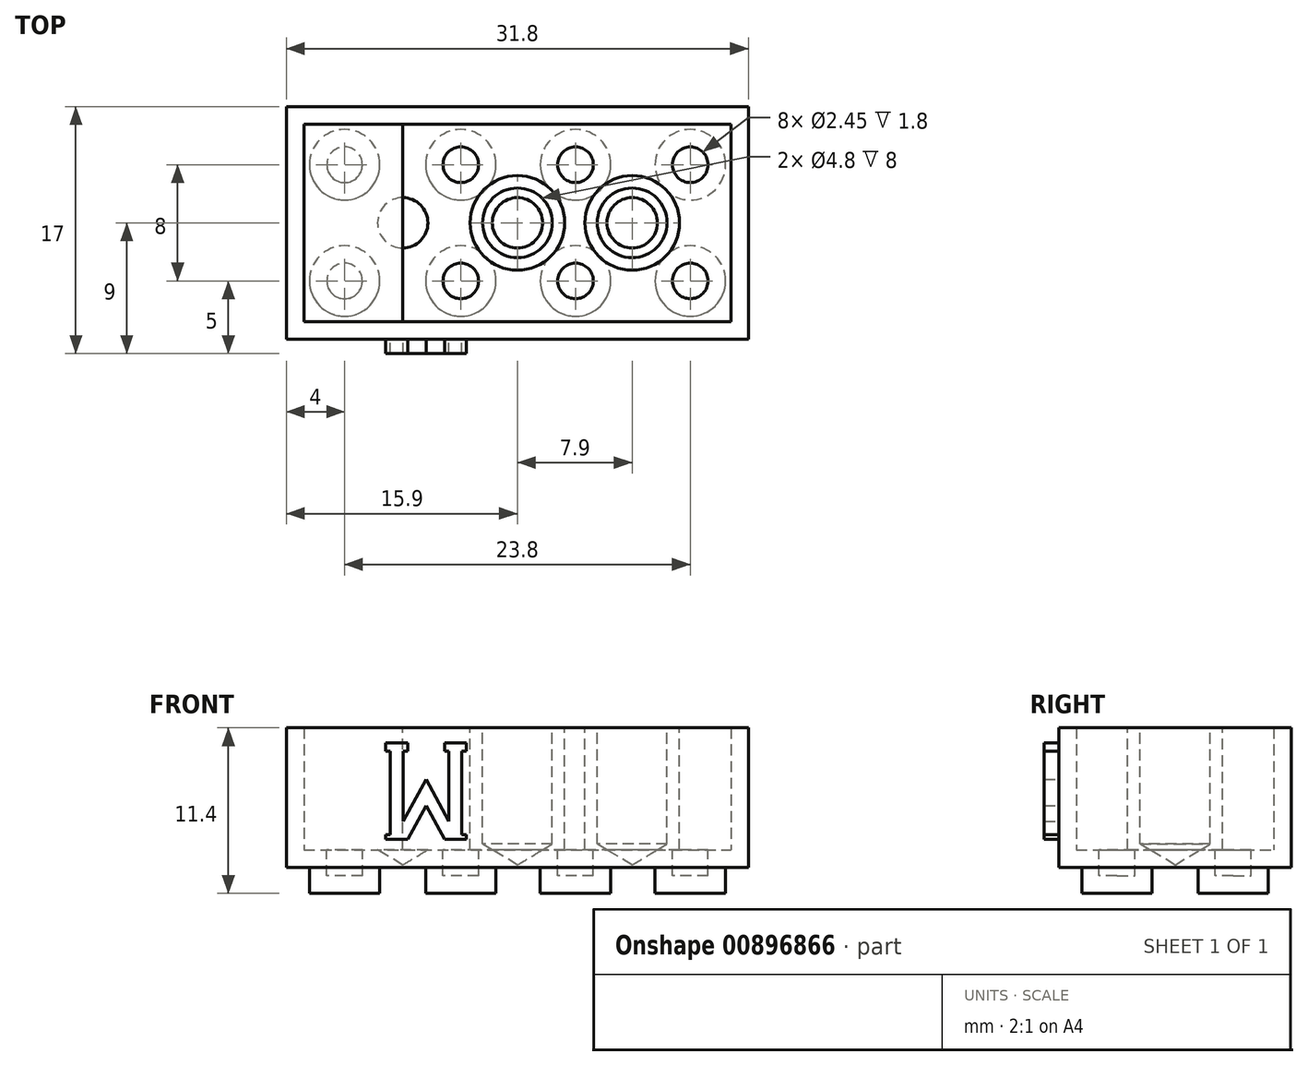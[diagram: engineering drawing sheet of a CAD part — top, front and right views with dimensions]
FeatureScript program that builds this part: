
annotation { "Feature Type Name" : "Feature", "Feature Type Description" : "" }
export const myFeature = defineFeature(function(context is Context, id is Id, definition is map)
    precondition{}
    {
        {
            var Q0;
            Q0=qCreatedBy(makeId("Front.planeOp"),FACE);
            var sketch = newSketch(context, id + "F0", { "sketchPlane" : qUnion([Q0])});
            skLineSegment(sketch, "E0.bottom", {"start": v(-9.6, 5.02) * mm, "end": v(22.2, 5.02) * mm});
            skLineSegment(sketch, "E0.top", {"start": v(-9.6, -4.58) * mm, "end": v(22.2, -4.58) * mm});
            skLineSegment(sketch, "E0.left", {"start": v(-9.6, 5.02) * mm, "end": v(-9.6, -4.58) * mm});
            skLineSegment(sketch, "E0.right", {"start": v(22.2, 5.02) * mm, "end": v(22.2, -4.58) * mm});
            skSolve(sketch);
        }
        {
            var Q0;
            Q0=makeQuery(id+"F0.imprint","IMPRINT",FACE,{"disambiguationData":[TD([[makeQuery(id+"F0.imprint","IMPRINT",EDGE,{"derivedFrom":sQuery(id+"F0.wireOp",EDGE,"E0.bottom")}),-1.0]])]});
            extrude(context, id + "F1", {"entities" : qUnion([Q0]), "depth" : 16 * mm, "offsetDistance" : 25 * mm});
        }
        {
            var Q0;
            Q0=makeQuery(id+"F1.opExtrude","SWEPT_FACE",FACE,{"disambiguationData":[OSD([sQuery(id+"F0.wireOp",EDGE,"E0.top")])]});
            var sketch = newSketch(context, id + "F2", { "sketchPlane" : qUnion([Q0])});
            skLineSegment(sketch, "E1", {"start": v(6.3, 0) * mm, "end": v(6.3, 16) * mm});
            skLineSegment(sketch, "E2", {"start": v(22.2, 8) * mm, "end": v(-9.6, 8) * mm});
            skLineSegment(sketch, "E3", {"start": v(14.2, 0) * mm, "end": v(14.2, 16) * mm});
            skLineSegment(sketch, "E4", {"start": v(-1.6, 0) * mm, "end": v(-1.6, 16) * mm});
            skLineSegment(sketch, "E5", {"start": v(22.2, 4) * mm, "end": v(20.62, 4) * mm});
            skLineSegment(sketch, "E6", {"start": v(22.22, 12) * mm, "end": v(20.62, 12) * mm});
            skCircle(sketch, "E7", {"center": v(18.2, 4) * mm, "radius": 2.43 * mm});
            skCircle(sketch, "E8", {"center": v(2.4, 4) * mm, "radius": 2.43 * mm});
            skCircle(sketch, "E9", {"center": v(18.2, 12) * mm, "radius": 2.43 * mm});
            skCircle(sketch, "E10", {"center": v(2.4, 12) * mm, "radius": 2.43 * mm});
            skCircle(sketch, "E11", {"center": v(10.3, 12) * mm, "radius": 2.43 * mm});
            skCircle(sketch, "E12", {"center": v(10.3, 4) * mm, "radius": 2.43 * mm});
            skCircle(sketch, "E13", {"center": v(-5.6, 4) * mm, "radius": 2.43 * mm});
            skCircle(sketch, "E14", {"center": v(-5.6, 12) * mm, "radius": 2.43 * mm});
            skLineSegment(sketch, "E15.trimOffspring", {"start": v(15.77, 4) * mm, "end": v(12.72, 4) * mm});
            skLineSegment(sketch, "E16.trimOffspring", {"start": v(7.87, 4) * mm, "end": v(4.82, 4) * mm});
            skLineSegment(sketch, "E17.trimOffspring", {"start": v(-0.03, 4) * mm, "end": v(-3.18, 4) * mm});
            skLineSegment(sketch, "E18.trimOffspring", {"start": v(-8.03, 4) * mm, "end": v(-9.6, 4) * mm});
            skLineSegment(sketch, "E19.trimOffspring", {"start": v(-8.03, 12) * mm, "end": v(-9.6, 12) * mm});
            skLineSegment(sketch, "E20.trimOffspring", {"start": v(-0.03, 12) * mm, "end": v(-3.18, 12) * mm});
            skLineSegment(sketch, "E21.trimOffspring", {"start": v(7.87, 12) * mm, "end": v(4.82, 12) * mm});
            skLineSegment(sketch, "E22.trimOffspring", {"start": v(15.77, 12) * mm, "end": v(12.72, 12) * mm});
            skSolve(sketch);
        }
        {
            var Q0;
            {var subQ0=sQuery(id+"F2.wireOp",EDGE,"E7");var subQ1=makeQuery(id+"F2.imprint","INTERSECT",VERTEX,{"derivedFrom":[sQuery(id+"F2.wireOp",EDGE,"E5"),subQ0]});Q0=makeQuery(id+"F2.imprint","IMPRINT",FACE,{"disambiguationData":[TD([[makeQuery(id+"F2.imprint","IMPRINT",EDGE,{"disambiguationData":[TD([[subQ1,-1.0]])],"derivedFrom":subQ0}),1.0]])]});}
            var Q1;
            {var subQ0=sQuery(id+"F2.wireOp",EDGE,"E12");var subQ1=makeQuery(id+"F2.imprint","INTERSECT",VERTEX,{"derivedFrom":[subQ0,sQuery(id+"F2.wireOp",EDGE,"E15.trimOffspring")]});Q1=makeQuery(id+"F2.imprint","IMPRINT",FACE,{"disambiguationData":[TD([[makeQuery(id+"F2.imprint","IMPRINT",EDGE,{"disambiguationData":[TD([[subQ1,-1.0]])],"derivedFrom":subQ0}),1.0]])]});}
            var Q2;
            {var subQ0=sQuery(id+"F2.wireOp",EDGE,"E8");var subQ1=makeQuery(id+"F2.imprint","INTERSECT",VERTEX,{"derivedFrom":[subQ0,sQuery(id+"F2.wireOp",EDGE,"E16.trimOffspring")]});Q2=makeQuery(id+"F2.imprint","IMPRINT",FACE,{"disambiguationData":[TD([[makeQuery(id+"F2.imprint","IMPRINT",EDGE,{"disambiguationData":[TD([[subQ1,-1.0]])],"derivedFrom":subQ0}),1.0]])]});}
            var Q3;
            {var subQ0=sQuery(id+"F2.wireOp",EDGE,"E13");var subQ1=makeQuery(id+"F2.imprint","INTERSECT",VERTEX,{"derivedFrom":[subQ0,sQuery(id+"F2.wireOp",EDGE,"E17.trimOffspring")]});Q3=makeQuery(id+"F2.imprint","IMPRINT",FACE,{"disambiguationData":[TD([[makeQuery(id+"F2.imprint","IMPRINT",EDGE,{"disambiguationData":[TD([[subQ1,-1.0]])],"derivedFrom":subQ0}),1.0]])]});}
            var Q4;
            {var subQ0=sQuery(id+"F2.wireOp",EDGE,"E14");var subQ1=makeQuery(id+"F2.imprint","INTERSECT",VERTEX,{"derivedFrom":[subQ0,sQuery(id+"F2.wireOp",EDGE,"E19.trimOffspring")]});Q4=makeQuery(id+"F2.imprint","IMPRINT",FACE,{"disambiguationData":[TD([[makeQuery(id+"F2.imprint","IMPRINT",EDGE,{"disambiguationData":[TD([[subQ1,1.0]])],"derivedFrom":subQ0}),1.0]])]});}
            var Q5;
            {var subQ0=sQuery(id+"F2.wireOp",EDGE,"E10");var subQ1=makeQuery(id+"F2.imprint","INTERSECT",VERTEX,{"derivedFrom":[subQ0,sQuery(id+"F2.wireOp",EDGE,"E20.trimOffspring")]});Q5=makeQuery(id+"F2.imprint","IMPRINT",FACE,{"disambiguationData":[TD([[makeQuery(id+"F2.imprint","IMPRINT",EDGE,{"disambiguationData":[TD([[subQ1,1.0]])],"derivedFrom":subQ0}),1.0]])]});}
            var Q6;
            {var subQ0=sQuery(id+"F2.wireOp",EDGE,"E11");var subQ1=makeQuery(id+"F2.imprint","INTERSECT",VERTEX,{"derivedFrom":[subQ0,sQuery(id+"F2.wireOp",EDGE,"E21.trimOffspring")]});Q6=makeQuery(id+"F2.imprint","IMPRINT",FACE,{"disambiguationData":[TD([[makeQuery(id+"F2.imprint","IMPRINT",EDGE,{"disambiguationData":[TD([[subQ1,1.0]])],"derivedFrom":subQ0}),1.0]])]});}
            var Q7;
            {var subQ0=sQuery(id+"F2.wireOp",EDGE,"E9");var subQ1=makeQuery(id+"F2.imprint","INTERSECT",VERTEX,{"derivedFrom":[sQuery(id+"F2.wireOp",EDGE,"E6"),subQ0]});Q7=makeQuery(id+"F2.imprint","IMPRINT",FACE,{"disambiguationData":[TD([[makeQuery(id+"F2.imprint","IMPRINT",EDGE,{"disambiguationData":[TD([[subQ1,-1.0]])],"derivedFrom":subQ0}),1.0]])]});}
            extrude(context, id + "F3", {"entities" : qUnion([Q0, Q1, Q2, Q3, Q4, Q5, Q6, Q7]), "operationType" : NewBodyOperationType.ADD, "depth" : 1.8 * mm, "offsetDistance" : 25 * mm});
        }
        {
            var Q0;
            Q0=makeQuery(id+"F1.opExtrude","SWEPT_FACE",FACE,{"disambiguationData":[OSD([sQuery(id+"F0.wireOp",EDGE,"E0.bottom")])]});
            var sketch = newSketch(context, id + "F4", { "sketchPlane" : qUnion([Q0])});
            skLineSegment(sketch, "E23", {"start": v(6.3, 0) * mm, "end": v(6.3, -16) * mm});
            skLineSegment(sketch, "E24", {"start": v(22.2, -8) * mm, "end": v(-9.6, -8) * mm});
            skLineSegment(sketch, "E25", {"start": v(-1.6, -16) * mm, "end": v(-1.6, 0) * mm});
            skLineSegment(sketch, "E26", {"start": v(14.2, -16) * mm, "end": v(14.2, 0) * mm});
            skLineSegment(sketch, "E27.bottom", {"start": v(-8.4, -1.2) * mm, "end": v(21, -1.2) * mm});
            skLineSegment(sketch, "E27.top", {"start": v(-8.4, -14.8) * mm, "end": v(21, -14.8) * mm});
            skLineSegment(sketch, "E27.left", {"start": v(-8.4, -1.2) * mm, "end": v(-8.4, -14.8) * mm});
            skLineSegment(sketch, "E27.right", {"start": v(21, -1.2) * mm, "end": v(21, -14.8) * mm});
            skPoint(sketch, "E27.middle", {"position": v(6.3, -8) * mm});
            skCircle(sketch, "E28", {"center": v(14.2, -8) * mm, "radius": 3.25 * mm});
            skCircle(sketch, "E29", {"center": v(6.3, -8) * mm, "radius": 3.25 * mm});
            skCircle(sketch, "E30", {"center": v(-1.6, -8) * mm, "radius": 3.25 * mm});
            skSolve(sketch);
        }
        {
            var Q0;
            Q0=makeQuery(id+"F1.opExtrude","SWEPT_FACE",FACE,{"disambiguationData":[OSD([sQuery(id+"F0.wireOp",EDGE,"E0.bottom")])]});
            shell(context, id + "F5", {"entities" : qUnion([Q0]), "thickness" : 1.2 * mm});
        }
        {
            var Q0;
            {var subQ0=sQuery(id+"F4.wireOp",EDGE,"E28");var subQ1=sQuery(id+"F4.wireOp",EDGE,"E24");var subQ2=makeQuery(id+"F4.imprint","INTERSECT",VERTEX,{"disambiguationData":[OD(0.0)],"derivedFrom":[subQ1,subQ0]});Q0=makeQuery(id+"F4.imprint","IMPRINT",FACE,{"disambiguationData":[TD([[makeQuery(id+"F4.imprint","IMPRINT",EDGE,{"disambiguationData":[TD([[subQ2,-1.0]])],"derivedFrom":subQ1}),-1.0]])]});}
            var Q1;
            {var subQ0=sQuery(id+"F4.wireOp",EDGE,"E28");var subQ1=sQuery(id+"F4.wireOp",EDGE,"E24");var subQ2=makeQuery(id+"F4.imprint","INTERSECT",VERTEX,{"disambiguationData":[OD(0.0)],"derivedFrom":[subQ1,subQ0]});Q1=makeQuery(id+"F4.imprint","IMPRINT",FACE,{"disambiguationData":[TD([[makeQuery(id+"F4.imprint","IMPRINT",EDGE,{"disambiguationData":[TD([[subQ2,-1.0]])],"derivedFrom":subQ1}),1.0]])]});}
            var Q2;
            {var subQ0=sQuery(id+"F4.wireOp",EDGE,"E26");var subQ1=sQuery(id+"F4.wireOp",EDGE,"E24");var subQ2=makeQuery(id+"F4.imprint","INTERSECT",VERTEX,{"derivedFrom":[subQ1,subQ0]});Q2=makeQuery(id+"F4.imprint","IMPRINT",FACE,{"disambiguationData":[TD([[makeQuery(id+"F4.imprint","IMPRINT",EDGE,{"disambiguationData":[TD([[subQ2,-1.0]])],"derivedFrom":subQ1}),1.0]])]});}
            var Q3;
            {var subQ0=sQuery(id+"F4.wireOp",EDGE,"E26");var subQ1=sQuery(id+"F4.wireOp",EDGE,"E24");var subQ2=makeQuery(id+"F4.imprint","INTERSECT",VERTEX,{"derivedFrom":[subQ1,subQ0]});Q3=makeQuery(id+"F4.imprint","IMPRINT",FACE,{"disambiguationData":[TD([[makeQuery(id+"F4.imprint","IMPRINT",EDGE,{"disambiguationData":[TD([[subQ2,-1.0]])],"derivedFrom":subQ1}),-1.0]])]});}
            var Q4;
            {var subQ0=sQuery(id+"F4.wireOp",EDGE,"E24");var subQ1=sQuery(id+"F4.wireOp",EDGE,"E23");var subQ2=makeQuery(id+"F4.imprint","INTERSECT",VERTEX,{"derivedFrom":[subQ1,subQ0]});Q4=makeQuery(id+"F4.imprint","IMPRINT",FACE,{"disambiguationData":[TD([[makeQuery(id+"F4.imprint","IMPRINT",EDGE,{"disambiguationData":[TD([[subQ2,-1.0]])],"derivedFrom":subQ1}),1.0]])]});}
            var Q5;
            {var subQ0=sQuery(id+"F4.wireOp",EDGE,"E24");var subQ1=sQuery(id+"F4.wireOp",EDGE,"E23");var subQ2=makeQuery(id+"F4.imprint","INTERSECT",VERTEX,{"derivedFrom":[subQ1,subQ0]});Q5=makeQuery(id+"F4.imprint","IMPRINT",FACE,{"disambiguationData":[TD([[makeQuery(id+"F4.imprint","IMPRINT",EDGE,{"disambiguationData":[TD([[subQ2,-1.0]])],"derivedFrom":subQ1}),-1.0]])]});}
            var Q6;
            {var subQ0=sQuery(id+"F4.wireOp",EDGE,"E29");var subQ1=sQuery(id+"F4.wireOp",EDGE,"E23");var subQ2=makeQuery(id+"F4.imprint","INTERSECT",VERTEX,{"disambiguationData":[OD(0.0)],"derivedFrom":[subQ1,subQ0]});Q6=makeQuery(id+"F4.imprint","IMPRINT",FACE,{"disambiguationData":[TD([[makeQuery(id+"F4.imprint","IMPRINT",EDGE,{"disambiguationData":[TD([[subQ2,-1.0]])],"derivedFrom":subQ1}),-1.0]])]});}
            var Q7;
            {var subQ0=sQuery(id+"F4.wireOp",EDGE,"E29");var subQ1=sQuery(id+"F4.wireOp",EDGE,"E23");var subQ2=makeQuery(id+"F4.imprint","INTERSECT",VERTEX,{"disambiguationData":[OD(0.0)],"derivedFrom":[subQ1,subQ0]});Q7=makeQuery(id+"F4.imprint","IMPRINT",FACE,{"disambiguationData":[TD([[makeQuery(id+"F4.imprint","IMPRINT",EDGE,{"disambiguationData":[TD([[subQ2,-1.0]])],"derivedFrom":subQ1}),1.0]])]});}
            var Q8;
            {var subQ0=sQuery(id+"F4.wireOp",EDGE,"E30");var subQ1=sQuery(id+"F4.wireOp",EDGE,"E24");var subQ2=makeQuery(id+"F4.imprint","INTERSECT",VERTEX,{"disambiguationData":[OD(0.0)],"derivedFrom":[subQ1,subQ0]});Q8=makeQuery(id+"F4.imprint","IMPRINT",FACE,{"disambiguationData":[TD([[makeQuery(id+"F4.imprint","IMPRINT",EDGE,{"disambiguationData":[TD([[subQ2,-1.0]])],"derivedFrom":subQ1}),1.0]])]});}
            var Q9;
            {var subQ0=sQuery(id+"F4.wireOp",EDGE,"E25");var subQ1=sQuery(id+"F4.wireOp",EDGE,"E24");var subQ2=makeQuery(id+"F4.imprint","INTERSECT",VERTEX,{"derivedFrom":[subQ1,subQ0]});Q9=makeQuery(id+"F4.imprint","IMPRINT",FACE,{"disambiguationData":[TD([[makeQuery(id+"F4.imprint","IMPRINT",EDGE,{"disambiguationData":[TD([[subQ2,-1.0]])],"derivedFrom":subQ1}),1.0]])]});}
            var Q10;
            {var subQ0=sQuery(id+"F4.wireOp",EDGE,"E25");var subQ1=sQuery(id+"F4.wireOp",EDGE,"E24");var subQ2=makeQuery(id+"F4.imprint","INTERSECT",VERTEX,{"derivedFrom":[subQ1,subQ0]});Q10=makeQuery(id+"F4.imprint","IMPRINT",FACE,{"disambiguationData":[TD([[makeQuery(id+"F4.imprint","IMPRINT",EDGE,{"disambiguationData":[TD([[subQ2,-1.0]])],"derivedFrom":subQ1}),-1.0]])]});}
            var Q11;
            {var subQ0=sQuery(id+"F4.wireOp",EDGE,"E30");var subQ1=sQuery(id+"F4.wireOp",EDGE,"E24");var subQ2=makeQuery(id+"F4.imprint","INTERSECT",VERTEX,{"disambiguationData":[OD(0.0)],"derivedFrom":[subQ1,subQ0]});Q11=makeQuery(id+"F4.imprint","IMPRINT",FACE,{"disambiguationData":[TD([[makeQuery(id+"F4.imprint","IMPRINT",EDGE,{"disambiguationData":[TD([[subQ2,-1.0]])],"derivedFrom":subQ1}),-1.0]])]});}
            extrude(context, id + "F6", {"entities" : qUnion([Q0, Q1, Q2, Q3, Q4, Q5, Q6, Q7, Q8, Q9, Q10, Q11]), "oppositeDirection" : true, "depth" : 8.4 * mm, "offsetDistance" : 25 * mm});
        }
        {
            var Q0;
            Q0=sQuery(id+"F4.wireOp",VERTEX,"E28.center");
            var Q1;
            Q1=makeQuery(id+"F1.opExtrude","SWEPT_BODY",BODY,{"disambiguationData":[OSD([sQuery(id+"F0.wireOp",EDGE,"E0.bottom"),sQuery(id+"F0.wireOp",EDGE,"E0.top"),sQuery(id+"F0.wireOp",EDGE,"E0.left"),sQuery(id+"F0.wireOp",EDGE,"E0.right")])]});
            var Q2;
            Q2=makeQuery(id+"F6.opExtrude","SWEPT_BODY",BODY,{"disambiguationData":[OSD([sQuery(id+"F4.wireOp",EDGE,"E28")])]});
            hole(context, id + "F7", {"style" : HoleStyle.SIMPLE, "endStyle" : HoleEndStyle.BLIND, "holeDiameter" : 4.8 * mm, "majorDiameter" : 5 * mm, "holeDepth" : 8 * mm, "isTappedThrough" : true, "tappedDepth" : 12 * mm, "tapClearance" : 3, "startFromSketch" : true, "locations" : qUnion([Q0]), "scope" : qUnion([Q1, Q2])});
        }
        {
            var Q0;
            Q0=sQuery(id+"F4.wireOp",VERTEX,"E27.middle");
            var Q1;
            Q1=makeQuery(id+"F1.opExtrude","SWEPT_BODY",BODY,{"disambiguationData":[OSD([sQuery(id+"F0.wireOp",EDGE,"E0.bottom"),sQuery(id+"F0.wireOp",EDGE,"E0.top"),sQuery(id+"F0.wireOp",EDGE,"E0.left"),sQuery(id+"F0.wireOp",EDGE,"E0.right")])]});
            var Q2;
            Q2=makeQuery(id+"F6.opExtrude","SWEPT_BODY",BODY,{"disambiguationData":[OSD([sQuery(id+"F4.wireOp",EDGE,"E29")])]});
            hole(context, id + "F8", {"style" : HoleStyle.SIMPLE, "endStyle" : HoleEndStyle.BLIND, "holeDiameter" : 4.8 * mm, "majorDiameter" : 5 * mm, "holeDepth" : 8 * mm, "isTappedThrough" : true, "tappedDepth" : 12 * mm, "tapClearance" : 3, "startFromSketch" : true, "locations" : qUnion([Q0]), "scope" : qUnion([Q1, Q2])});
        }
        {
            var Q0;
            Q0=sQuery(id+"F4.wireOp",VERTEX,"E30.center");
            var Q1;
            Q1=makeQuery(id+"F1.opExtrude","SWEPT_BODY",BODY,{"disambiguationData":[OSD([sQuery(id+"F0.wireOp",EDGE,"E0.bottom"),sQuery(id+"F0.wireOp",EDGE,"E0.top"),sQuery(id+"F0.wireOp",EDGE,"E0.left"),sQuery(id+"F0.wireOp",EDGE,"E0.right")])]});
            var Q2;
            Q2=makeQuery(id+"F6.opExtrude","SWEPT_BODY",BODY,{"disambiguationData":[OSD([sQuery(id+"F4.wireOp",EDGE,"E30")])]});
            hole(context, id + "F9", {"style" : HoleStyle.SIMPLE, "endStyle" : HoleEndStyle.BLIND, "holeDiameter" : 4.8 * mm, "majorDiameter" : 5 * mm, "holeDepth" : 8 * mm, "isTappedThrough" : true, "tappedDepth" : 12 * mm, "tapClearance" : 3, "startFromSketch" : true, "locations" : qUnion([Q0]), "scope" : qUnion([Q1, Q2])});
        }
        {
            var Q0;
            Q0=makeQuery(id+"F1.opExtrude","CAP_FACE",FACE,{"disambiguationData":[OSD([sQuery(id+"F0.wireOp",EDGE,"E0.bottom"),sQuery(id+"F0.wireOp",EDGE,"E0.top"),sQuery(id+"F0.wireOp",EDGE,"E0.left"),sQuery(id+"F0.wireOp",EDGE,"E0.right")])],"isStart":false});
            var sketch = newSketch(context, id + "F10", { "sketchPlane" : qUnion([Q0])});
            skLineSegment(sketch, "E31", {"start": v(1.26, 3.96) * mm, "end": v(1.26, 3.4) * mm});
            skLineSegment(sketch, "E32", {"start": v(1.26, 3.4) * mm, "end": v(1.57, 3.4) * mm});
            skLineSegment(sketch, "E33", {"start": v(1.57, 3.4) * mm, "end": v(1.57, -1.41) * mm});
            skLineSegment(sketch, "E34", {"start": v(1.57, -1.41) * mm, "end": v(0, 1.47) * mm});
            skLineSegment(sketch, "E35", {"start": v(0, 1.47) * mm, "end": v(-1.57, -1.41) * mm});
            skLineSegment(sketch, "E36", {"start": v(-1.57, -1.41) * mm, "end": v(-1.57, 3.4) * mm});
            skLineSegment(sketch, "E37", {"start": v(-1.57, 3.4) * mm, "end": v(-1.26, 3.4) * mm});
            skLineSegment(sketch, "E38", {"start": v(-1.26, 3.4) * mm, "end": v(-1.26, 3.96) * mm});
            skLineSegment(sketch, "E39", {"start": v(-1.26, 3.96) * mm, "end": v(-2.78, 3.96) * mm});
            skLineSegment(sketch, "E40", {"start": v(-2.78, 3.96) * mm, "end": v(-2.78, 3.4) * mm});
            skLineSegment(sketch, "E41", {"start": v(-2.78, 3.4) * mm, "end": v(-2.47, 3.4) * mm});
            skLineSegment(sketch, "E42", {"start": v(-2.47, 3.4) * mm, "end": v(-2.47, -2.34) * mm});
            skLineSegment(sketch, "E43", {"start": v(-2.47, -2.34) * mm, "end": v(-2.78, -2.34) * mm});
            skLineSegment(sketch, "E44", {"start": v(-2.78, -2.34) * mm, "end": v(-2.78, -2.67) * mm});
            skLineSegment(sketch, "E45", {"start": v(-2.78, -2.67) * mm, "end": v(-1.26, -2.67) * mm});
            skLineSegment(sketch, "E46", {"start": v(-1.26, -2.67) * mm, "end": v(0, -0.35) * mm});
            skLineSegment(sketch, "E47", {"start": v(0, -0.35) * mm, "end": v(1.26, -2.67) * mm});
            skLineSegment(sketch, "E48", {"start": v(1.26, -2.67) * mm, "end": v(2.78, -2.67) * mm});
            skLineSegment(sketch, "E49", {"start": v(2.78, -2.67) * mm, "end": v(2.78, -2.34) * mm});
            skLineSegment(sketch, "E50", {"start": v(2.78, -2.34) * mm, "end": v(2.47, -2.34) * mm});
            skLineSegment(sketch, "E51", {"start": v(2.47, -2.34) * mm, "end": v(2.47, 3.4) * mm});
            skLineSegment(sketch, "E52", {"start": v(2.47, 3.4) * mm, "end": v(2.78, 3.4) * mm});
            skLineSegment(sketch, "E53", {"start": v(2.78, 3.4) * mm, "end": v(2.78, 3.96) * mm});
            skLineSegment(sketch, "E54", {"start": v(2.78, 3.96) * mm, "end": v(1.26, 3.96) * mm});
            skSolve(sketch);
        }
        {
            var Q0;
            Q0=makeQuery(id+"F10.imprint","IMPRINT",FACE,{"disambiguationData":[TD([[makeQuery(id+"F10.imprint","IMPRINT",EDGE,{"derivedFrom":sQuery(id+"F10.wireOp",EDGE,"E31")}),1.0]])]});
            extrude(context, id + "F11", {"entities" : qUnion([Q0]), "operationType" : NewBodyOperationType.ADD, "depth" : 1 * mm, "offsetDistance" : 25 * mm});
        }
    });
